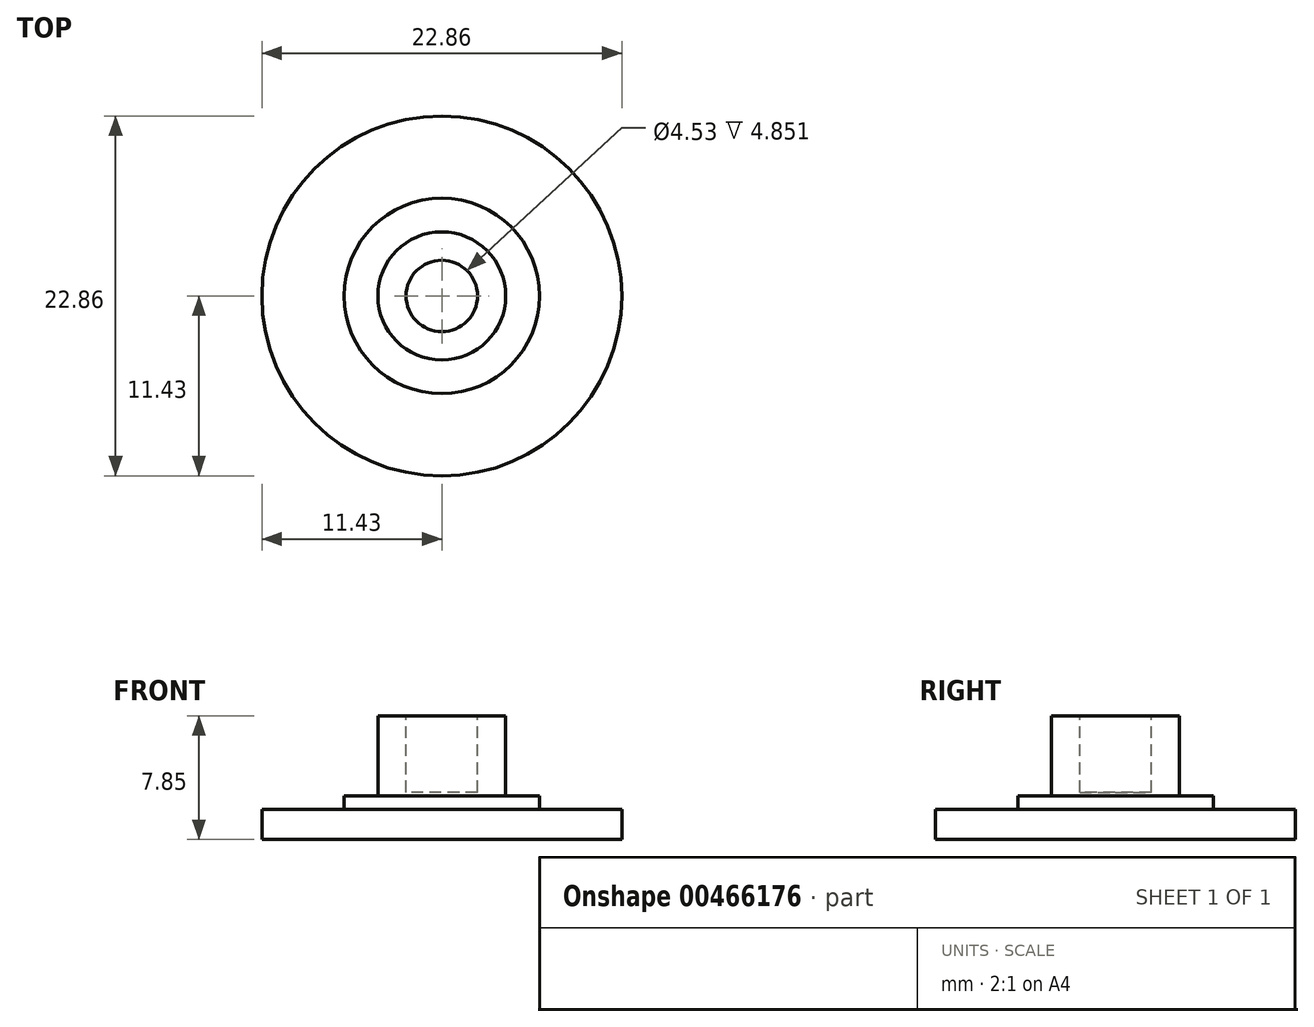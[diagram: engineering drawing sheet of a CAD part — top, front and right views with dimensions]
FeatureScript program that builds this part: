
annotation { "Feature Type Name" : "Feature", "Feature Type Description" : "" }
export const myFeature = defineFeature(function(context is Context, id is Id, definition is map)
    precondition{}
    {
        {
            var Q0;
            Q0=qCreatedBy(makeId("Top.planeOp"),FACE);
            var sketch = newSketch(context, id + "F0", { "sketchPlane" : qUnion([Q0])});
            skCircle(sketch, "E0", {"center": v(0, 0) * mm, "radius": 11.43 * mm});
            skSolve(sketch);
        }
        {
            var Q0;
            Q0=makeQuery(id+"F0.imprint","IMPRINT",FACE,{"disambiguationData":[TD([[makeQuery(id+"F0.imprint","IMPRINT",EDGE,{"derivedFrom":sQuery(id+"F0.wireOp",EDGE,"E0")}),1.0]])]});
            extrude(context, id + "F1", {"entities" : qUnion([Q0]), "depth" : 1.9 * mm});
        }
        {
            var Q0;
            Q0=makeQuery(id+"F1.opExtrude","CAP_FACE",FACE,{"disambiguationData":[OSD([sQuery(id+"F0.wireOp",EDGE,"E0")])],"isStart":false});
            var sketch = newSketch(context, id + "F2", { "sketchPlane" : qUnion([Q0])});
            skCircle(sketch, "E1", {"center": v(0, 0) * mm, "radius": 6.2 * mm});
            skSolve(sketch);
        }
        {
            var Q0;
            Q0 = qSketchRegion(id + "F2", true);
            extrude(context, id + "F3", {"entities" : qUnion([Q0]), "operationType" : NewBodyOperationType.ADD, "depth" : 0.86 * mm});
        }
        {
            var Q0;
            Q0=makeQuery(id+"F3.opExtrude","CAP_FACE",FACE,{"disambiguationData":[OSD([sQuery(id+"F2.wireOp",EDGE,"E1")])],"isStart":false});
            var sketch = newSketch(context, id + "F4", { "sketchPlane" : qUnion([Q0])});
            skCircle(sketch, "E2", {"center": v(0, 0) * mm, "radius": 4.06 * mm});
            skSolve(sketch);
        }
        {
            var Q0;
            Q0=makeQuery(id+"F4.imprint","IMPRINT",FACE,{"disambiguationData":[TD([[makeQuery(id+"F4.imprint","IMPRINT",EDGE,{"derivedFrom":sQuery(id+"F4.wireOp",EDGE,"E2")}),1.0]])]});
            extrude(context, id + "F5", {"entities" : qUnion([Q0]), "operationType" : NewBodyOperationType.ADD, "depth" : 5.08 * mm});
        }
        {
            var Q0;
            Q0=makeQuery(id+"F5.opExtrude","CAP_FACE",FACE,{"disambiguationData":[OSD([sQuery(id+"F4.wireOp",EDGE,"E2")])],"isStart":false});
            var sketch = newSketch(context, id + "F6", { "sketchPlane" : qUnion([Q0])});
            skCircle(sketch, "E3", {"center": v(0, 0) * mm, "radius": 2.27 * mm});
            skSolve(sketch);
        }
        {
            var Q0;
            Q0 = qSketchRegion(id + "F6", true);
            extrude(context, id + "F7", {"entities" : qUnion([Q0]), "operationType" : NewBodyOperationType.REMOVE, "oppositeDirection" : true, "depth" : 4.85 * mm});
        }
    });
